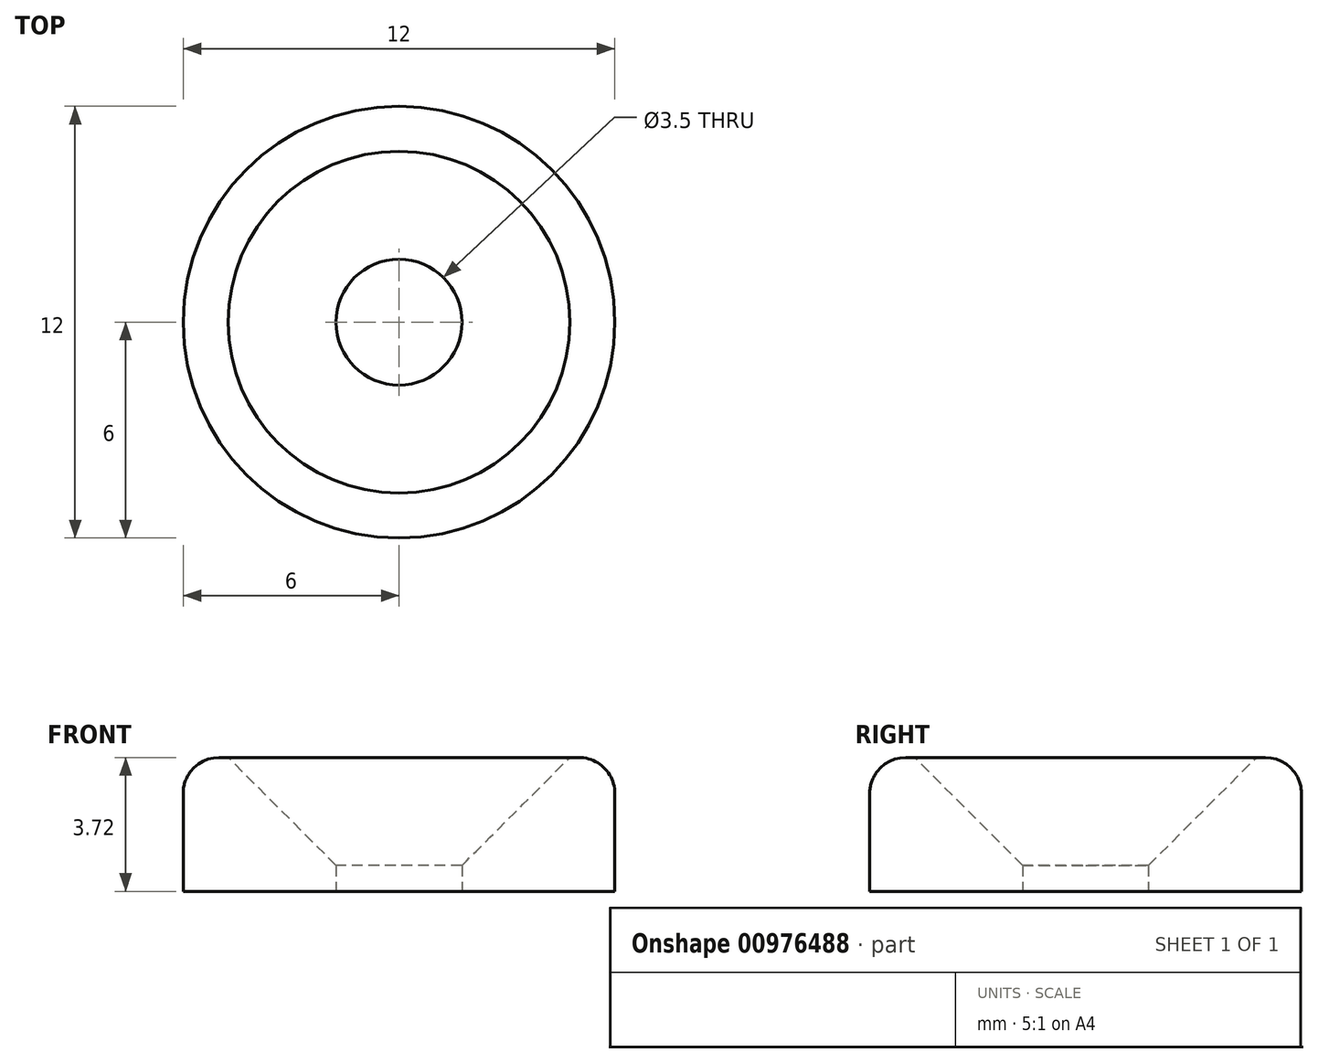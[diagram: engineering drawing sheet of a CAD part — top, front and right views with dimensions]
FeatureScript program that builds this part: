
annotation { "Feature Type Name" : "Feature", "Feature Type Description" : "" }
export const myFeature = defineFeature(function(context is Context, id is Id, definition is map)
    precondition{}
    {
        {
            var Q0;
            Q0=qCreatedBy(makeId("Top.planeOp"),FACE);
            var sketch = newSketch(context, id + "F0", { "sketchPlane" : qUnion([Q0])});
            skCircle(sketch, "E0", {"center": v(0, 0) * mm, "radius": 6 * mm});
            skCircle(sketch, "E1", {"center": v(0, 0) * mm, "radius": 4 * mm});
            skCircle(sketch, "E2", {"center": v(0, 0) * mm, "radius": 1.75 * mm});
            skSolve(sketch);
        }
        {
            var Q0;
            Q0=makeQuery(id+"F0.imprint","IMPRINT",FACE,{"disambiguationData":[TD([[makeQuery(id+"F0.imprint","IMPRINT",EDGE,{"derivedFrom":sQuery(id+"F0.wireOp",EDGE,"E0")}),1.0]])]});
            var Q1;
            Q1=makeQuery(id+"F0.imprint","IMPRINT",FACE,{"disambiguationData":[TD([[makeQuery(id+"F0.imprint","IMPRINT",EDGE,{"derivedFrom":sQuery(id+"F0.wireOp",EDGE,"E1")}),1.0]])]});
            extrude(context, id + "F1", {"entities" : qUnion([Q0, Q1]), "depth" : 6 * mm, "offsetDistance" : 25 * mm});
        }
        {
            var Q0;
            Q0=makeQuery(id+"F1.opExtrude","CAP_EDGE",EDGE,{"disambiguationData":[OSD([sQuery(id+"F0.wireOp",EDGE,"E0")])],"isStart":false});
            fillet(context, id + "F2", {"entities" : qUnion([Q0]), "radius" : 1 * mm, "tangentPropagation" : true, "allowEdgeOverflow" : false});
        }
        {
            var Q0;
            Q0=makeQuery(id+"F1.opExtrude","CAP_EDGE",EDGE,{"disambiguationData":[OSD([sQuery(id+"F0.wireOp",EDGE,"E2")])],"isStart":false});
            chamfer(context, id + "F3", {"entities" : qUnion([Q0]), "width" : 3 * mm, "tangentPropagation" : true});
        }
        {
            var Q0;
            Q0=makeQuery(id+"F1.opExtrude","CAP_FACE",FACE,{"disambiguationData":[OSD([sQuery(id+"F0.wireOp",EDGE,"E0"),sQuery(id+"F0.wireOp",EDGE,"E2")])],"isStart":true});
            extrude(context, id + "F4", {"entities" : qUnion([Q0]), "operationType" : NewBodyOperationType.REMOVE, "oppositeDirection" : true, "depth" : 2.28 * mm, "offsetDistance" : 25 * mm});
        }
    });
